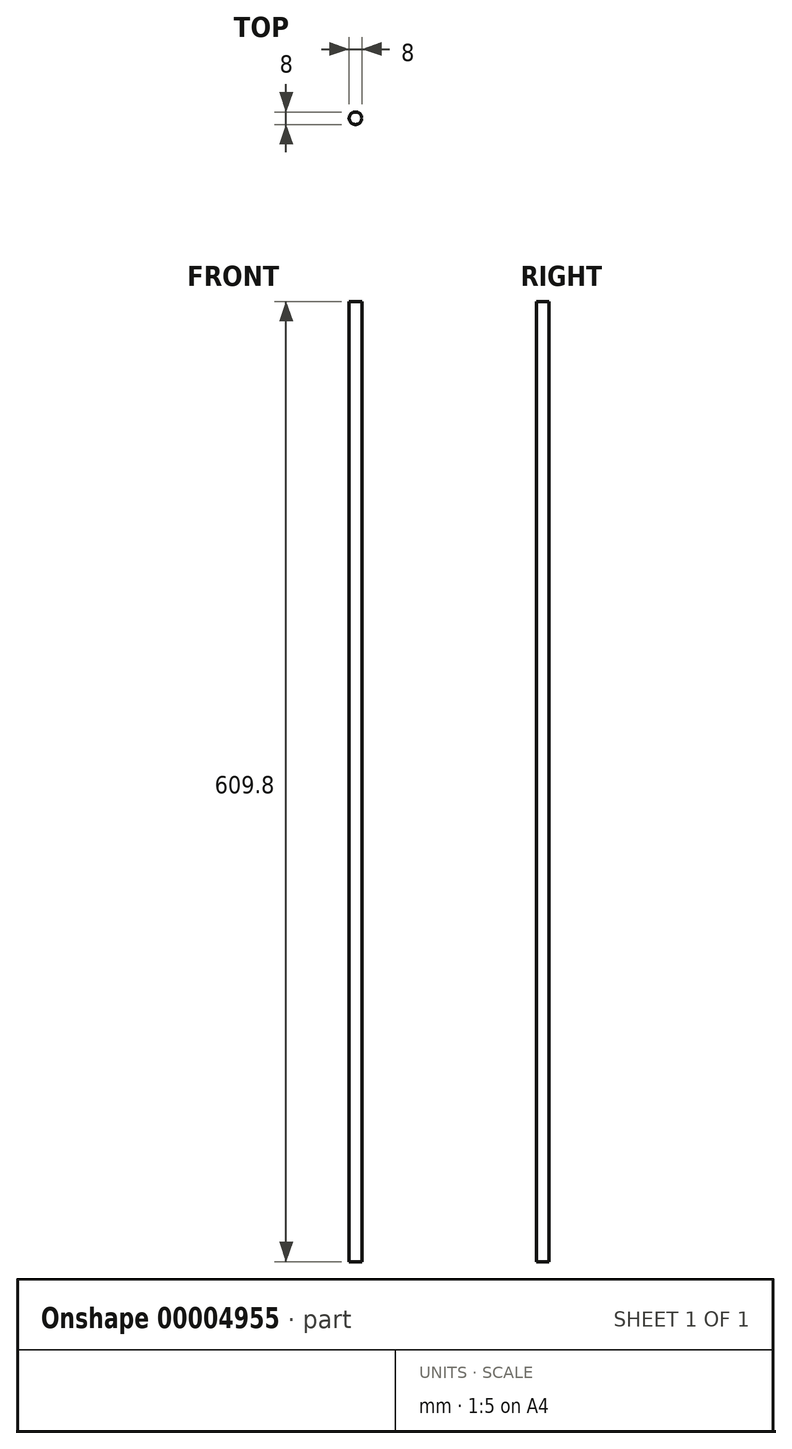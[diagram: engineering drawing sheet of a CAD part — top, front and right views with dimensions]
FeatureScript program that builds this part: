
annotation { "Feature Type Name" : "Feature", "Feature Type Description" : "" }
export const myFeature = defineFeature(function(context is Context, id is Id, definition is map)
    precondition{}
    {
        {
            var Q0;
            Q0=qCreatedBy(makeId("Top.planeOp"),FACE);
            var sketch = newSketch(context, id + "F0", { "sketchPlane" : qUnion([Q0])});
            skCircle(sketch, "E0", {"center": v(0, 0) * mm, "radius": 4 * mm});
            skSolve(sketch);
        }
        {
            var Q0;
            Q0 = qSketchRegion(id + "F0", true);
            extrude(context, id + "F1", {"entities" : qUnion([Q0]), "depth" : 609.8 * mm, "symmetric" : true});
        }
    });
